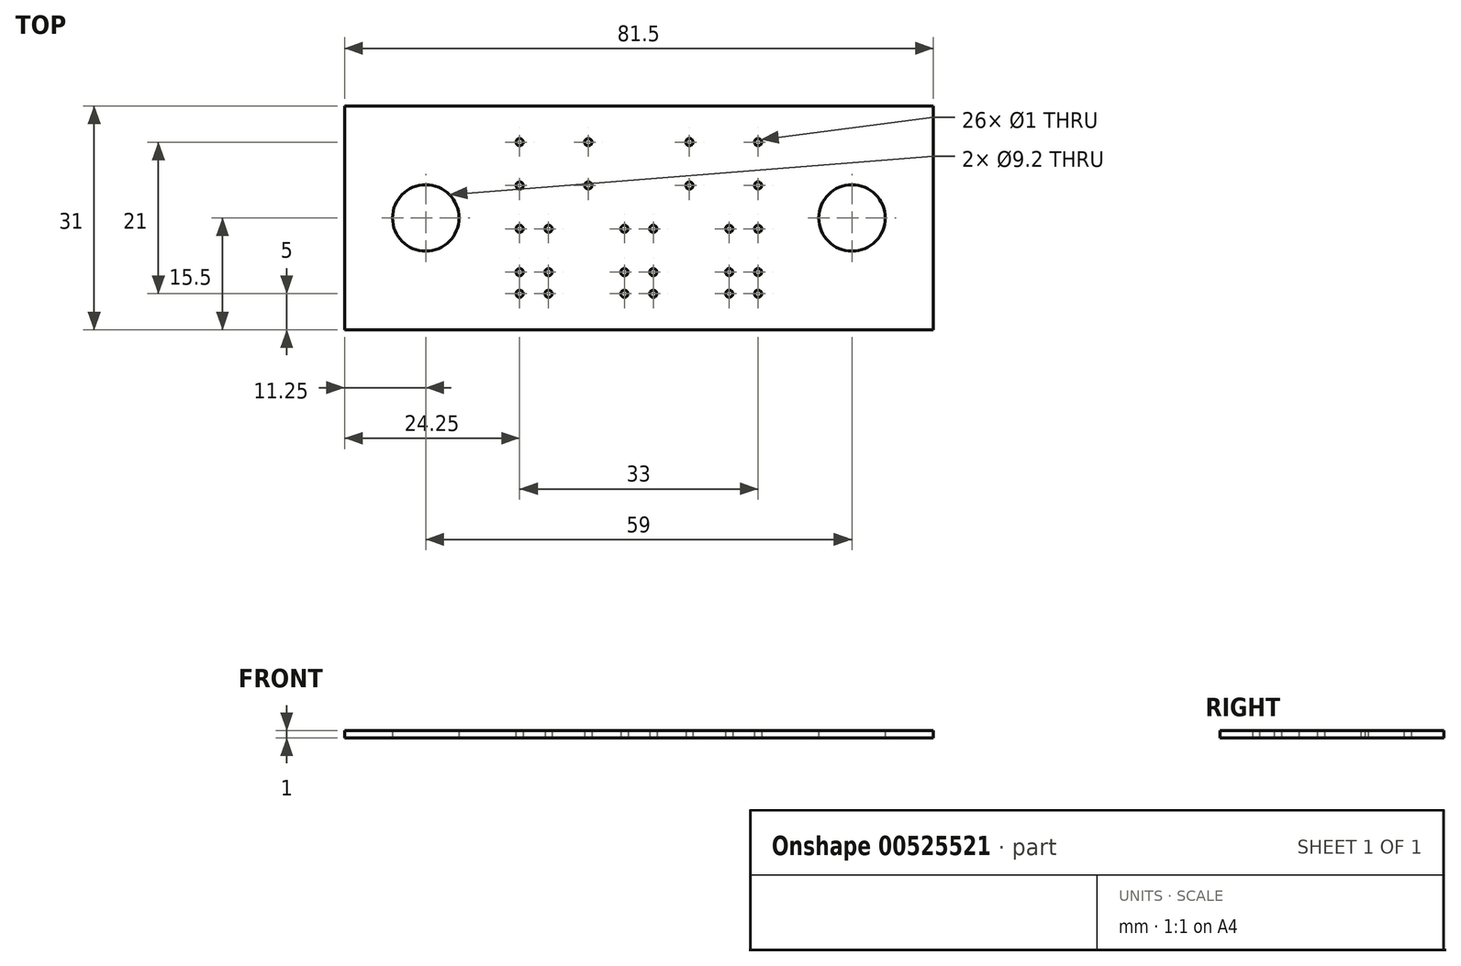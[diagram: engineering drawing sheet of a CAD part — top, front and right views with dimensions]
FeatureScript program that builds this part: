
annotation { "Feature Type Name" : "Feature", "Feature Type Description" : "" }
export const myFeature = defineFeature(function(context is Context, id is Id, definition is map)
    precondition{}
    {
        {
            var Q0;
            Q0=qCreatedBy(makeId("Top.planeOp"),FACE);
            var sketch = newSketch(context, id + "F0", { "sketchPlane" : qUnion([Q0])});
            skCircle(sketch, "E0", {"center": v(0, 0) * mm, "radius": 4.6 * mm});
            skCircle(sketch, "E1", {"center": v(0, 0) * mm, "radius": 6.25 * mm, "construction": true});
            skCircle(sketch, "E2.1.0.0", {"center": v(59, 0) * mm, "radius": 6.25 * mm, "construction": true});
            skCircle(sketch, "E2.1.0.1", {"center": v(59, 0) * mm, "radius": 4.6 * mm});
            skLineSegment(sketch, "E2.direction1", {"start": v(0, 0) * mm, "end": v(59, 0) * mm, "construction": true});
            skLineSegment(sketch, "E3.bottom", {"start": v(10, 10.5) * mm, "end": v(13, 10.5) * mm, "construction": true});
            skLineSegment(sketch, "E3.top", {"start": v(10, 4.5) * mm, "end": v(25.5, 4.5) * mm, "construction": true});
            skLineSegment(sketch, "E3.left", {"start": v(10, 10.5) * mm, "end": v(10, 4.5) * mm, "construction": true});
            skLineSegment(sketch, "E3.right", {"start": v(25.5, 10.5) * mm, "end": v(25.5, 4.5) * mm, "construction": true});
            skLineSegment(sketch, "E4.bottom", {"start": v(33.5, 10.5) * mm, "end": v(36.5, 10.5) * mm, "construction": true});
            skLineSegment(sketch, "E4.top", {"start": v(33.5, 4.5) * mm, "end": v(49, 4.5) * mm, "construction": true});
            skLineSegment(sketch, "E4.left", {"start": v(33.5, 10.5) * mm, "end": v(33.5, 4.5) * mm, "construction": true});
            skLineSegment(sketch, "E4.right", {"start": v(49, 10.5) * mm, "end": v(49, 4.5) * mm, "construction": true});
            skLineSegment(sketch, "E5", {"start": v(13, 10.5) * mm, "end": v(13, 4.5) * mm, "construction": true});
            skLineSegment(sketch, "E6", {"start": v(22.5, 4.5) * mm, "end": v(22.5, 10.5) * mm, "construction": true});
            skLineSegment(sketch, "E7", {"start": v(36.5, 10.5) * mm, "end": v(36.5, 4.5) * mm, "construction": true});
            skLineSegment(sketch, "E8", {"start": v(46, 4.5) * mm, "end": v(46, 10.5) * mm, "construction": true});
            skLineSegment(sketch, "E9", {"start": v(13, 10.5) * mm, "end": v(22.5, 10.5) * mm, "construction": true});
            skLineSegment(sketch, "E10", {"start": v(22.5, 10.5) * mm, "end": v(25.5, 10.5) * mm, "construction": true});
            skLineSegment(sketch, "E11", {"start": v(36.5, 10.5) * mm, "end": v(46, 10.5) * mm, "construction": true});
            skLineSegment(sketch, "E12", {"start": v(46, 10.5) * mm, "end": v(49, 10.5) * mm, "construction": true});
            skCircle(sketch, "E13", {"center": v(13, -1.5) * mm, "radius": 0.5 * mm});
            skCircle(sketch, "E14", {"center": v(13, -10.5) * mm, "radius": 0.5 * mm});
            skLineSegment(sketch, "E15", {"start": v(13, -1.5) * mm, "end": v(13, -10.5) * mm, "construction": true});
            skCircle(sketch, "E16", {"center": v(13, -7.5) * mm, "radius": 0.5 * mm});
            skCircle(sketch, "E17", {"center": v(17, -1.5) * mm, "radius": 0.5 * mm});
            skCircle(sketch, "E18", {"center": v(17, -7.5) * mm, "radius": 0.5 * mm});
            skCircle(sketch, "E19", {"center": v(17, -10.5) * mm, "radius": 0.5 * mm});
            skLineSegment(sketch, "E20", {"start": v(13, -1.5) * mm, "end": v(17, -1.5) * mm, "construction": true});
            skLineSegment(sketch, "E21", {"start": v(17, -1.5) * mm, "end": v(17, -10.5) * mm, "construction": true});
            skLineSegment(sketch, "E22", {"start": v(13, -10.5) * mm, "end": v(17, -10.5) * mm, "construction": true});
            skLineSegment(sketch, "E23.1.0.0", {"start": v(27.5, -1.5) * mm, "end": v(31.5, -1.5) * mm, "construction": true});
            skLineSegment(sketch, "E23.1.0.1", {"start": v(27.5, -10.5) * mm, "end": v(31.5, -10.5) * mm, "construction": true});
            skLineSegment(sketch, "E23.1.0.2", {"start": v(27.5, -1.5) * mm, "end": v(27.5, -10.5) * mm, "construction": true});
            skLineSegment(sketch, "E23.1.0.3", {"start": v(31.5, -1.5) * mm, "end": v(31.5, -10.5) * mm, "construction": true});
            skCircle(sketch, "E23.1.0.4", {"center": v(31.5, -7.5) * mm, "radius": 0.5 * mm});
            skCircle(sketch, "E23.1.0.5", {"center": v(27.5, -7.5) * mm, "radius": 0.5 * mm});
            skCircle(sketch, "E23.1.0.6", {"center": v(27.5, -1.5) * mm, "radius": 0.5 * mm});
            skCircle(sketch, "E23.1.0.7", {"center": v(31.5, -10.5) * mm, "radius": 0.5 * mm});
            skCircle(sketch, "E23.1.0.8", {"center": v(31.5, -1.5) * mm, "radius": 0.5 * mm});
            skCircle(sketch, "E23.1.0.9", {"center": v(27.5, -10.5) * mm, "radius": 0.5 * mm});
            skLineSegment(sketch, "E23.2.0.0", {"start": v(42, -1.5) * mm, "end": v(46, -1.5) * mm, "construction": true});
            skLineSegment(sketch, "E23.2.0.1", {"start": v(42, -10.5) * mm, "end": v(46, -10.5) * mm, "construction": true});
            skLineSegment(sketch, "E23.2.0.2", {"start": v(42, -1.5) * mm, "end": v(42, -10.5) * mm, "construction": true});
            skLineSegment(sketch, "E23.2.0.3", {"start": v(46, -1.5) * mm, "end": v(46, -10.5) * mm, "construction": true});
            skCircle(sketch, "E23.2.0.4", {"center": v(46, -7.5) * mm, "radius": 0.5 * mm});
            skCircle(sketch, "E23.2.0.5", {"center": v(42, -7.5) * mm, "radius": 0.5 * mm});
            skCircle(sketch, "E23.2.0.6", {"center": v(42, -1.5) * mm, "radius": 0.5 * mm});
            skCircle(sketch, "E23.2.0.7", {"center": v(46, -10.5) * mm, "radius": 0.5 * mm});
            skCircle(sketch, "E23.2.0.8", {"center": v(46, -1.5) * mm, "radius": 0.5 * mm});
            skCircle(sketch, "E23.2.0.9", {"center": v(42, -10.5) * mm, "radius": 0.5 * mm});
            skLineSegment(sketch, "E23.direction1", {"start": v(13, -10.5) * mm, "end": v(27.5, -10.5) * mm, "construction": true});
            skLineSegment(sketch, "E24", {"start": v(25.5, 4.5) * mm, "end": v(33.5, 4.5) * mm, "construction": true});
            skLineSegment(sketch, "E25", {"start": v(29.5, 4.5) * mm, "end": v(29.5, 0) * mm, "construction": true});
            skPoint(sketch, "E26", {"position": v(29.5, -1.5) * mm});
            skCircle(sketch, "E27", {"center": v(13, 4.5) * mm, "radius": 0.5 * mm});
            skCircle(sketch, "E28", {"center": v(22.5, 10.5) * mm, "radius": 0.5 * mm});
            skCircle(sketch, "E29", {"center": v(36.5, 4.5) * mm, "radius": 0.5 * mm});
            skCircle(sketch, "E30", {"center": v(46, 10.5) * mm, "radius": 0.5 * mm});
            skCircle(sketch, "E31", {"center": v(13, 10.5) * mm, "radius": 0.5 * mm});
            skCircle(sketch, "E32", {"center": v(22.5, 4.5) * mm, "radius": 0.5 * mm});
            skCircle(sketch, "E33", {"center": v(36.5, 10.5) * mm, "radius": 0.5 * mm});
            skCircle(sketch, "E34", {"center": v(46, 4.5) * mm, "radius": 0.5 * mm});
            skLineSegment(sketch, "E35", {"start": v(44, -10.5) * mm, "end": v(44, 10.5) * mm, "construction": true});
            skPoint(sketch, "E36", {"position": v(44, 0) * mm});
            skLineSegment(sketch, "E37.bottom", {"start": v(-11.25, -15.5) * mm, "end": v(70.25, -15.5) * mm});
            skLineSegment(sketch, "E37.top", {"start": v(-11.25, 15.5) * mm, "end": v(70.25, 15.5) * mm});
            skLineSegment(sketch, "E37.left", {"start": v(-11.25, -15.5) * mm, "end": v(-11.25, 15.5) * mm});
            skLineSegment(sketch, "E37.right", {"start": v(70.25, -15.5) * mm, "end": v(70.25, 15.5) * mm});
            skLineSegment(sketch, "E38", {"start": v(-6.25, 0) * mm, "end": v(-11.25, 0) * mm, "construction": true});
            skLineSegment(sketch, "E39", {"start": v(44, 10.5) * mm, "end": v(44, 15.5) * mm, "construction": true});
            skLineSegment(sketch, "E40", {"start": v(65.25, 0) * mm, "end": v(70.25, 0) * mm, "construction": true});
            skLineSegment(sketch, "E41", {"start": v(44, -10.5) * mm, "end": v(44, -15.5) * mm, "construction": true});
            skSolve(sketch);
        }
        {
            var Q0;
            Q0 = qSketchRegion(id + "F0", true);
            extrude(context, id + "F1", {"entities" : qUnion([Q0]), "depth" : 1 * mm, "offsetDistance" : 25 * mm});
        }
    });
